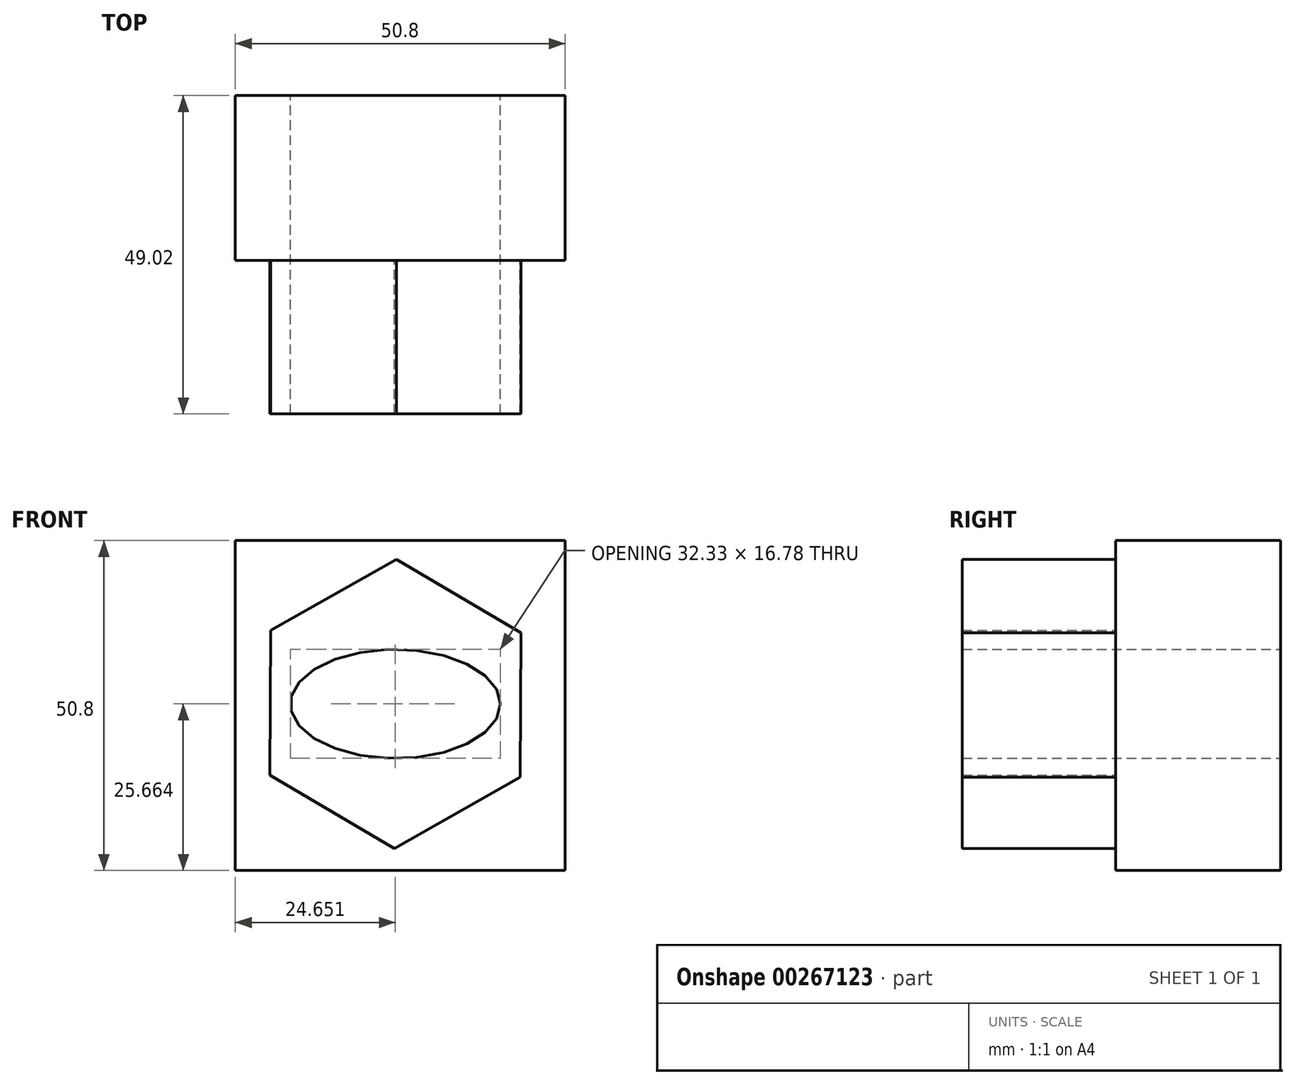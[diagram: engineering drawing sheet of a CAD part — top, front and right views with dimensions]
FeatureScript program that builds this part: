
annotation { "Feature Type Name" : "Feature", "Feature Type Description" : "" }
export const myFeature = defineFeature(function(context is Context, id is Id, definition is map)
    precondition{}
    {
        {
            var Q0;
            Q0=qCreatedBy(makeId("Front.planeOp"),FACE);
            var sketch = newSketch(context, id + "F0", { "sketchPlane" : qUnion([Q0])});
            skLineSegment(sketch, "E0.bottom", {"start": v(-51.22, 63.12) * mm, "end": v(-0.42, 63.12) * mm});
            skLineSegment(sketch, "E0.top", {"start": v(-51.22, 12.32) * mm, "end": v(-0.42, 12.32) * mm});
            skLineSegment(sketch, "E0.left", {"start": v(-51.22, 63.12) * mm, "end": v(-51.22, 12.32) * mm});
            skLineSegment(sketch, "E0.right", {"start": v(-0.42, 63.12) * mm, "end": v(-0.42, 12.32) * mm});
            skLineSegment(sketch, "E1.0", {"start": v(-7.4, 26.7) * mm, "end": v(-26.75, 15.73) * mm});
            skLineSegment(sketch, "E1.1", {"start": v(-26.75, 15.73) * mm, "end": v(-45.93, 27.02) * mm});
            skLineSegment(sketch, "E1.2", {"start": v(-45.93, 27.02) * mm, "end": v(-45.75, 49.27) * mm});
            skLineSegment(sketch, "E1.3", {"start": v(-45.75, 49.27) * mm, "end": v(-26.38, 60.24) * mm});
            skLineSegment(sketch, "E1.4", {"start": v(-26.38, 60.24) * mm, "end": v(-7.2, 48.95) * mm});
            skLineSegment(sketch, "E1.5", {"start": v(-7.2, 48.95) * mm, "end": v(-7.4, 26.7) * mm});
            skPoint(sketch, "E1.0.midPoint", {"position": v(-17.07, 21.21) * mm});
            skEllipse(sketch, "E2", {"center": v(-26.57, 37.98) * mm, "majorRadius": 16.16 * mm, "minorRadius": 8.4 * mm, "majorAxis": v(1, 0)});
            skSolve(sketch);
        }
        {
            var Q0;
            Q0=makeQuery(id+"F0.imprint","IMPRINT",FACE,{"disambiguationData":[TD([[makeQuery(id+"F0.imprint","IMPRINT",EDGE,{"derivedFrom":sQuery(id+"F0.wireOp",EDGE,"E0.bottom")}),-1.0]])]});
            extrude(context, id + "F1", {"entities" : qUnion([Q0]), "depth" : 25.4 * mm});
        }
        {
            var Q0;
            Q0=makeQuery(id+"F0.imprint","IMPRINT",FACE,{"disambiguationData":[TD([[makeQuery(id+"F0.imprint","IMPRINT",EDGE,{"derivedFrom":sQuery(id+"F0.wireOp",EDGE,"E1.0")}),-1.0]])]});
            extrude(context, id + "F2", {"entities" : qUnion([Q0]), "operationType" : NewBodyOperationType.ADD, "depth" : 49.02 * mm});
        }
    });
